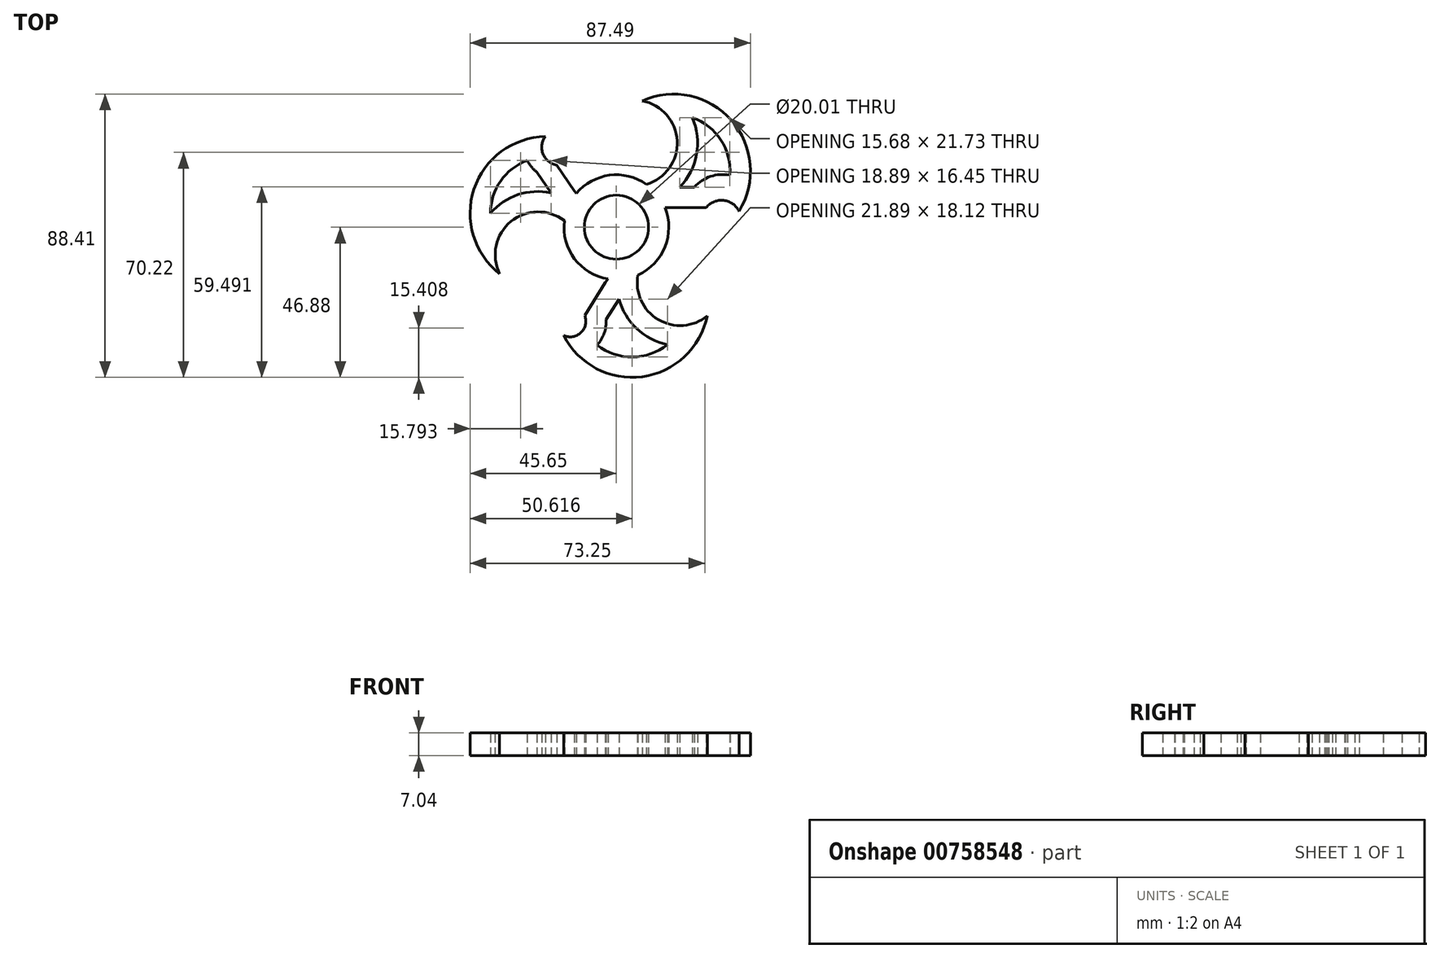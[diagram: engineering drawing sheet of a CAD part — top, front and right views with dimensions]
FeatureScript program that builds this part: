
annotation { "Feature Type Name" : "Feature", "Feature Type Description" : "" }
export const myFeature = defineFeature(function(context is Context, id is Id, definition is map)
    precondition{}
    {
        {
            var Q0;
            Q0=qCreatedBy(makeId("Top.planeOp"),FACE);
            var sketch = newSketch(context, id + "F0", { "sketchPlane" : qUnion([Q0])});
            skCircle(sketch, "E0", {"center": v(0, 0) * mm, "radius": 10 * mm});
            skArc(sketch, "E1", {"start": v(8.64, 13.2) * mm, "mid": v(19, 26.54) * mm, "end": v(8.06, 39.43) * mm});
            skArc(sketch, "E2", {"start": v(38.26, 4.98) * mm, "mid": v(35.9, 33.37) * mm, "end": v(8.06, 39.43) * mm});
            skLineSegment(sketch, "E3", {"start": v(28.06, 6.12) * mm, "end": v(15.94, 6.12) * mm});
            skArc(sketch, "E4", {"start": v(-15.57, 1.47) * mm, "mid": v(-32.58, 2.03) * mm, "end": v(-36.43, -14.55) * mm});
            skArc(sketch, "E5", {"start": v(-22.2, 28.29) * mm, "mid": v(-44.43, 11.89) * mm, "end": v(-36.43, -14.55) * mm});
            skLineSegment(sketch, "E6", {"start": v(-18.62, 19.38) * mm, "end": v(-13.14, 11.35) * mm});
            skArc(sketch, "E7", {"start": v(7.16, -13.16) * mm, "mid": v(12.32, -28.35) * mm, "end": v(28.35, -27.71) * mm});
            skArc(sketch, "E8", {"start": v(-16.48, -33.77) * mm, "mid": v(8.09, -46.67) * mm, "end": v(28.35, -27.71) * mm});
            skArc(sketch, "E9", {"start": v(-16.48, -33.77) * mm, "mid": v(-11.07, -32.92) * mm, "end": v(-9.85, -27.58) * mm});
            skLineSegment(sketch, "E10", {"start": v(-9.85, -27.58) * mm, "end": v(-3.46, -17.28) * mm});
            skLineSegment(sketch, "E11", {"start": v(-13.14, 11.35) * mm, "end": v(-12.49, 10.43) * mm});
            skLineSegment(sketch, "E12", {"start": v(-15.57, 1.47) * mm, "end": v(-14.96, 0.57) * mm});
            skLineSegment(sketch, "E13", {"start": v(-3.46, -17.28) * mm, "end": v(-2.55, -16.15) * mm});
            skCircle(sketch, "E14.0", {"center": v(0, 0) * mm, "radius": 16.35 * mm});
            skLineSegment(sketch, "E15", {"start": v(15.94, 6.12) * mm, "end": v(15.16, 6.12) * mm});
            skLineSegment(sketch, "E16", {"start": v(-2.55, -16.15) * mm, "end": v(-2.55, -16.15) * mm});
            skLineSegment(sketch, "E17", {"start": v(-2.55, -16.15) * mm, "end": v(-2.54, -16.15) * mm});
            skLineSegment(sketch, "E18.0", {"start": v(-24.8, 17.18) * mm, "end": v(-20.41, 10.74) * mm});
            skArc(sketch, "E18.1", {"start": v(-27.84, 20.83) * mm, "mid": v(-26.52, 18.84) * mm, "end": v(-24.8, 17.18) * mm});
            skArc(sketch, "E18.2", {"start": v(-27.84, 20.83) * mm, "mid": v(-36.14, 14.4) * mm, "end": v(-39.3, 4.39) * mm});
            skArc(sketch, "E18.3", {"start": v(-20.41, 10.74) * mm, "mid": v(-30.72, 10.12) * mm, "end": v(-39.3, 4.39) * mm});
            skLineSegment(sketch, "E19.0", {"start": v(24.38, 12.47) * mm, "end": v(19.76, 12.47) * mm});
            skArc(sketch, "E19.1", {"start": v(35.44, 16.2) * mm, "mid": v(29.4, 15.85) * mm, "end": v(24.38, 12.47) * mm});
            skArc(sketch, "E19.2", {"start": v(35.44, 16.2) * mm, "mid": v(32.63, 27.21) * mm, "end": v(23.68, 34.2) * mm});
            skArc(sketch, "E19.3", {"start": v(19.76, 12.47) * mm, "mid": v(25.04, 22.74) * mm, "end": v(23.68, 34.2) * mm});
            skLineSegment(sketch, "E20.0", {"start": v(-3.18, -28.87) * mm, "end": v(0.82, -22.41) * mm});
            skArc(sketch, "E20.1", {"start": v(-5.98, -36.78) * mm, "mid": v(-3.81, -33.1) * mm, "end": v(-3.18, -28.87) * mm});
            skArc(sketch, "E20.2", {"start": v(-5.98, -36.78) * mm, "mid": v(4.99, -40.53) * mm, "end": v(15.91, -36.65) * mm});
            skArc(sketch, "E20.3", {"start": v(0.82, -22.41) * mm, "mid": v(6.35, -31.67) * mm, "end": v(15.91, -36.65) * mm});
            skArc(sketch, "E21", {"start": v(-22.2, 28.29) * mm, "mid": v(-22.89, 22.84) * mm, "end": v(-18.62, 19.38) * mm});
            skArc(sketch, "E22", {"start": v(38.26, 4.98) * mm, "mid": v(33.47, 8.37) * mm, "end": v(28.06, 6.12) * mm});
            skSolve(sketch);
        }
        {
            var Q0;
            Q0 = qSketchRegion(id + "F0", true);
            extrude(context, id + "F1", {"entities" : qUnion([Q0]), "depth" : 7.04 * mm, "offsetDistance" : 25.4 * mm});
        }
    });
